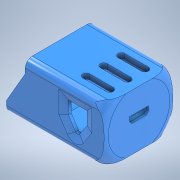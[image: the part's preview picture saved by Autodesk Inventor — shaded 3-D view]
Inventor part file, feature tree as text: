
AUTODESK INVENTOR PART (.ipt)
format: ipt  version: 2020 (Build 240168000, 168)  size: 564,224 bytes
history: native  units: in
note: dims shown in document units (in); Inventor stores cm internally (conversion verified against a paired STEP export)
features: extrude x13, sketch x7, chamfer x6, fillet x5, other x3, revolve x2, projected_geometry x2, mirror x1, plane x1, boolean_combine x1
ambient origin geometry x8: Origin, YZ Plane, XZ Plane, XY Plane, X Axis, Y Axis, Z Axis, Center Point
bodies: Solid4 (feature_tree), Solid2 (feature_tree)
feature tree (41):
  other  "SmartEgg Housing Main.ipt"
  extrude  "Extrusion1"  Depth=0.3937in
  extrude  "Extrusion2"  Depth=0.0492in TaperAngle=0.0deg
  extrude  "Extrusion3"  Depth=0.0394in
  fillet  "Fillet1"  Radius=0.0787in
  fillet  "Fillet2"  Radius=0.1181in
  fillet  "Fillet3"  Radius=0.0787in
  fillet  "Fillet4"  Radius=0.5659in
  sketch  "Sketch5"  dims[d5=0.0394in d6=0.0in d7=0.0394in d8=0.0787in d9=0.1181in d10=0.0787in d11=0.5659in d12=0.0in]
  extrude  "Extrusion6"  TaperAngle=0.0deg  [1 undecoded]
  extrude  "Extrusion7"  Depth=0.0394in
  extrude  "Extrusion8"  TaperAngle=45.0deg  [1 undecoded]
  chamfer  "Chamfer2"  Distance=0.0394in
  fillet  "Fillet5"  Radius=0.0394in
  extrude  "Extrusion13"  Depth=0.0591in
  mirror  "Mirror1"
  extrude  "Extrusion4"  Depth=0.1181in
  extrude  "Extrusion5"  Depth=0.3937in TaperAngle=0.0deg
  chamfer  "Chamfer1"  Distance=0.0354in
  extrude  "Extrusion9"  TaperAngle=0.0deg  [1 undecoded]
  chamfer  "Chamfer7"  Distance=0.1476in
  chamfer  "Chamfer8"  Distance=0.0591in
  chamfer  "Chamfer9"  Angle=45.0deg  [1 undecoded]
  chamfer  "Chamfer10"  Distance=0.0591in
  sketch  "Sketch7"  dims[d16=0.0394in d17=0.0787in d18=45.0deg d19=0.4528in]
  sketch  "Sketch8"  dims[d20=0.0787in d23=45.0deg]
  plane  "Work Plane2"
  other  "Housing Largest Area"
  revolve  "Revolution1"  [1 undecoded]
  revolve  "Revolution2"  [1 undecoded]
  extrude  "Extrusion10"  Depth=0.1181in TaperAngle=0.0deg
  boolean_combine  "Combine1"
  sketch  "Sketch10"  dims[d24=45.0deg d25=0.0394in d26=0.0394in d31=0.0591in d32=0.1969in d33=0.3937in d34=0.0in d35=0.0354in d36=0.0in d37=0.1476in d38=0.0in d39=0.0591in d40=0.0354in d41=45.0deg d42=0.0591in d43=0.0394in d58=0.1181in d59=0.5659in d60=0.0in d62=0.0394in d63=0.1181in d64=0.0394in d65=75.0deg d66=0.1181in d67=0.0394in d68=75.0deg d69=0.1181in d70=0.0394in d71=75.0deg d72=0.1181in d73=0.0394in d74=75.0deg d75=90.0deg d76=0.1772in d77=90.0deg d78=0.1378in d79=360.0deg d80=0.9744in d81=0.0in d83=0.0591in d84=0.0591in d85=0.0591in d86=0.5906in d87=0.3937in d88=0.3937in d89=0.1181in d90=0.0in d91=0.1181in d92=0.0in d93=0.0787in d94=0.0in d95=0.1181in]
  extrude  "Extrusion11"  Depth=0.0394in
  extrude  "Extrusion12"  Depth=0.1181in TaperAngle=75.0deg
  sketch  "Sketch3"  dims[d0=0.3937in d1=0.4872in]
  other  "ESP32 Feather"
  sketch  "Sketch4"  dims[d2=0.0in d3=0.0492in d4=0.0in]
  sketch  "Sketch6"  dims[d13=0.315in d14=0.0in d15=0.0in]
  projected_geometry  "Project Cut Edges1"
  projected_geometry  "Project Cut Edges2"
note: 6 required parameter values undecoded (feature->parameter linkage not recoverable at this tier; creation-order binding heuristic only, values carry confidence <= 0.55)